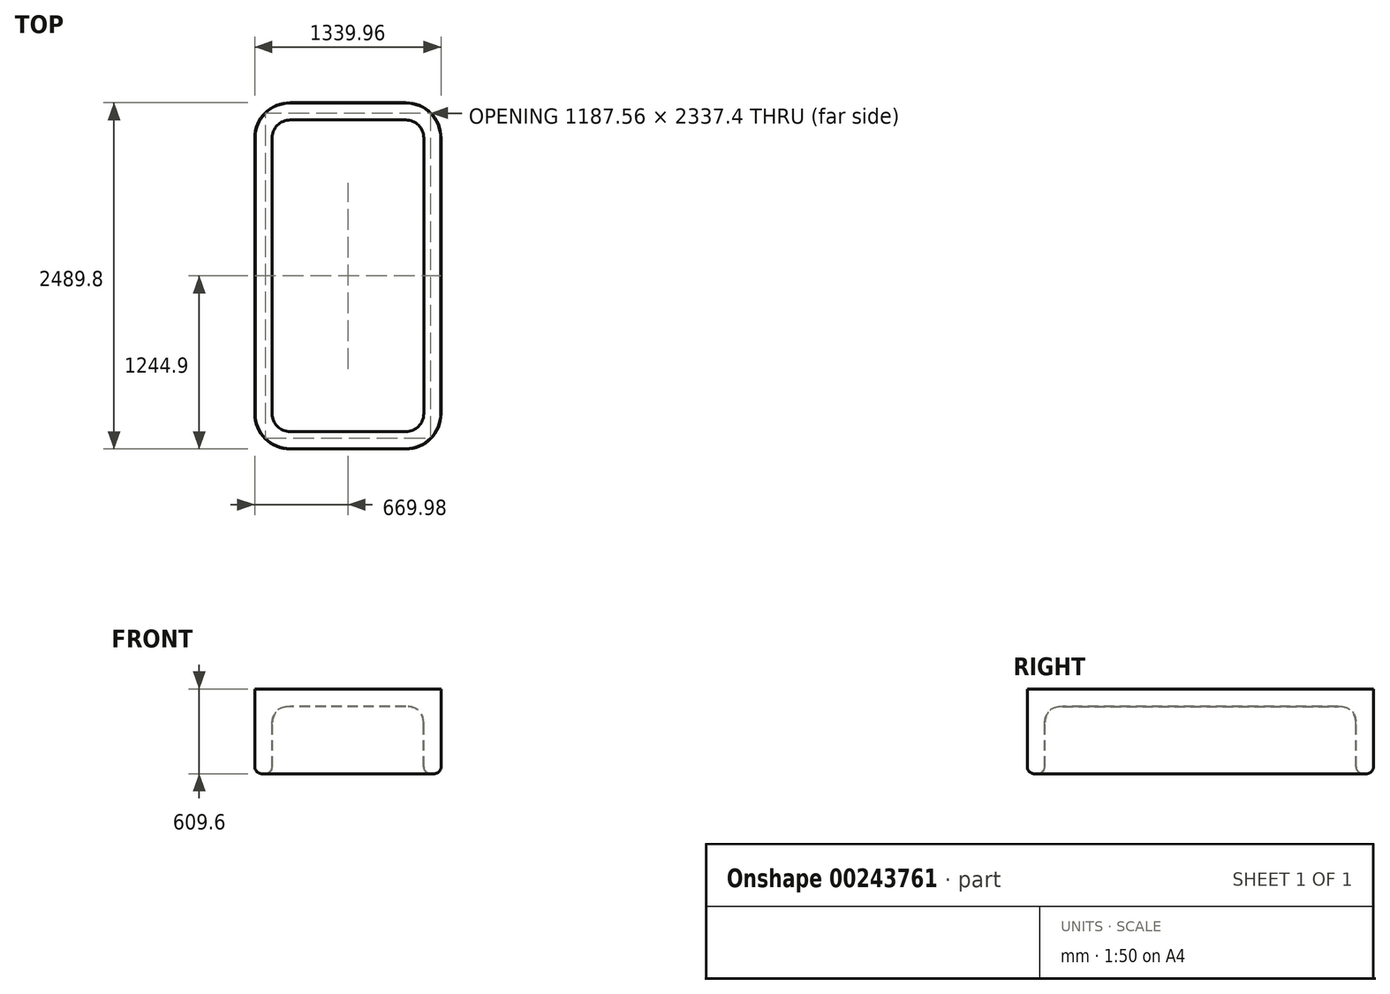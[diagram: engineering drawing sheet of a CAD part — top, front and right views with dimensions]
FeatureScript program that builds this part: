
annotation { "Feature Type Name" : "Feature", "Feature Type Description" : "" }
export const myFeature = defineFeature(function(context is Context, id is Id, definition is map)
    precondition{}
    {
        {
            var Q0;
            Q0=qCreatedBy(makeId("Top.planeOp"),FACE);
            var sketch = newSketch(context, id + "F0", { "sketchPlane" : qUnion([Q0])});
            skLineSegment(sketch, "E0.bottom", {"start": v(661.36, 66.56) * mm, "end": v(-678.6, 66.56) * mm});
            skLineSegment(sketch, "E0.top", {"start": v(661.36, 2556.36) * mm, "end": v(-678.6, 2556.36) * mm});
            skLineSegment(sketch, "E0.left", {"start": v(661.36, 66.56) * mm, "end": v(661.36, 2556.36) * mm});
            skLineSegment(sketch, "E0.right", {"start": v(-678.6, 66.56) * mm, "end": v(-678.6, 2556.36) * mm});
            skPoint(sketch, "E1.firstSnap0", {"position": v(-8.62, 66.56) * mm});
            skLineSegment(sketch, "E1.bottom", {"start": v(-8.62, 25.77) * mm, "end": v(-8.62, 25.77) * mm});
            skLineSegment(sketch, "E1.top", {"start": v(-8.62, 66.56) * mm, "end": v(-8.62, 66.56) * mm});
            skLineSegment(sketch, "E1.left", {"start": v(-8.62, 25.77) * mm, "end": v(-8.62, 66.56) * mm});
            skLineSegment(sketch, "E1.right", {"start": v(-8.62, 25.77) * mm, "end": v(-8.62, 66.56) * mm});
            skLineSegment(sketch, "E2.bottom", {"start": v(-14.24, -12.86) * mm, "end": v(-8.62, -12.86) * mm});
            skLineSegment(sketch, "E2.top", {"start": v(-14.24, 51.34) * mm, "end": v(-8.62, 51.34) * mm});
            skLineSegment(sketch, "E2.left", {"start": v(-14.24, -12.86) * mm, "end": v(-14.24, 51.34) * mm});
            skLineSegment(sketch, "E2.right", {"start": v(-8.62, -12.86) * mm, "end": v(-8.62, 51.34) * mm});
            skSolve(sketch);
        }
        {
            var Q0;
            Q0=makeQuery(id+"F0.imprint","IMPRINT",FACE,{"disambiguationData":[TD([[makeQuery(id+"F0.imprint","IMPRINT",EDGE,{"derivedFrom":sQuery(id+"F0.wireOp",EDGE,"E0.top")}),1.0]])]});
            extrude(context, id + "F1", {"entities" : qUnion([Q0]), "oppositeDirection" : true, "depth" : 609.6 * mm});
        }
        {
            var Q0;
            Q0=makeQuery(id+"F1.opExtrude","CAP_FACE",FACE,{"disambiguationData":[OSD([sQuery(id+"F0.wireOp",EDGE,"E0.bottom"),sQuery(id+"F0.wireOp",EDGE,"E0.top"),sQuery(id+"F0.wireOp",EDGE,"E0.left"),sQuery(id+"F0.wireOp",EDGE,"E0.right")])],"isStart":false});
            shell(context, id + "F2", {"entities" : qUnion([Q0]), "thickness" : 127 * mm});
        }
        {
            var Q0;
            Q0=makeQuery(id+"F2.opShell","OFFSET_EDGE",EDGE,{"disambiguationData":[OSD([sQuery(id+"F0.wireOp",EDGE,"E0.bottom"),sQuery(id+"F0.wireOp",EDGE,"E0.left")])]});
            var Q1;
            Q1=makeQuery(id+"F2.opShell","OFFSET_EDGE",EDGE,{"disambiguationData":[OSD([sQuery(id+"F0.wireOp",EDGE,"E0.top"),sQuery(id+"F0.wireOp",EDGE,"E0.left")])]});
            var Q2;
            Q2=makeQuery(id+"F2.opShell","OFFSET_EDGE",EDGE,{"disambiguationData":[OSD([sQuery(id+"F0.wireOp",EDGE,"E0.bottom"),sQuery(id+"F0.wireOp",EDGE,"E0.right")])]});
            var Q3;
            Q3=makeQuery(id+"F2.opShell","OFFSET_EDGE",EDGE,{"disambiguationData":[OSD([sQuery(id+"F0.wireOp",EDGE,"E0.top"),sQuery(id+"F0.wireOp",EDGE,"E0.right")])]});
            fillet(context, id + "F3", {"entities" : qUnion([Q0, Q1, Q2, Q3]), "radius" : 127 * mm, "tangentPropagation" : true, "allowEdgeOverflow" : false});
        }
        {
            var Q0;
            {var subQ0=sQuery(id+"F0.wireOp",EDGE,"E0.top");Q0=makeQuery(id+"F2.opShell","OFFSET_EDGE",EDGE,{"disambiguationData":[OSD([subQ0]),TDD([makeQuery(id+"F1.opExtrude","CAP_EDGE",EDGE,{"disambiguationData":[OSD([subQ0])],"isStart":true})])]});}
            fillet(context, id + "F4", {"entities" : qUnion([Q0]), "radius" : 127 * mm, "tangentPropagation" : true, "rho" : 0.5, "crossSection" : FilletCrossSection.CONIC, "allowEdgeOverflow" : false});
        }
        {
            var Q0;
            Q0=makeQuery(id+"F1.opExtrude","CAP_EDGE",EDGE,{"disambiguationData":[OSD([sQuery(id+"F0.wireOp",EDGE,"E0.top")])],"isStart":false});
            var Q1;
            Q1=makeQuery(id+"F1.opExtrude","CAP_EDGE",EDGE,{"disambiguationData":[OSD([sQuery(id+"F0.wireOp",EDGE,"E0.left")])],"isStart":false});
            var Q2;
            Q2=makeQuery(id+"F1.opExtrude","CAP_EDGE",EDGE,{"disambiguationData":[OSD([sQuery(id+"F0.wireOp",EDGE,"E0.bottom")])],"isStart":false});
            var Q3;
            Q3=makeQuery(id+"F1.opExtrude","CAP_EDGE",EDGE,{"disambiguationData":[OSD([sQuery(id+"F0.wireOp",EDGE,"E0.right")])],"isStart":false});
            var Q4;
            {var subQ0=sQuery(id+"F0.wireOp",EDGE,"E0.top");Q4=makeQuery(id+"F2.opShell","OFFSET_EDGE",EDGE,{"disambiguationData":[OSD([subQ0]),TDD([makeQuery(id+"F1.opExtrude","CAP_EDGE",EDGE,{"disambiguationData":[OSD([subQ0])],"isStart":false})])]});}
            fillet(context, id + "F5", {"entities" : qUnion([Q0, Q1, Q2, Q3, Q4]), "radius" : 50.8 * mm, "tangentPropagation" : true, "allowEdgeOverflow" : false});
        }
        {
            var Q0;
            Q0=makeQuery(id+"F1.opExtrude","SWEPT_EDGE",EDGE,{"disambiguationData":[OSD([sQuery(id+"F0.wireOp",EDGE,"E0.bottom"),sQuery(id+"F0.wireOp",EDGE,"E0.right")])]});
            var Q1;
            Q1=makeQuery(id+"F1.opExtrude","SWEPT_EDGE",EDGE,{"disambiguationData":[OSD([sQuery(id+"F0.wireOp",EDGE,"E0.bottom"),sQuery(id+"F0.wireOp",EDGE,"E0.left")])]});
            var Q2;
            Q2=makeQuery(id+"F1.opExtrude","SWEPT_EDGE",EDGE,{"disambiguationData":[OSD([sQuery(id+"F0.wireOp",EDGE,"E0.top"),sQuery(id+"F0.wireOp",EDGE,"E0.left")])]});
            var Q3;
            Q3=makeQuery(id+"F1.opExtrude","SWEPT_EDGE",EDGE,{"disambiguationData":[OSD([sQuery(id+"F0.wireOp",EDGE,"E0.top"),sQuery(id+"F0.wireOp",EDGE,"E0.right")])]});
            fillet(context, id + "F6", {"entities" : qUnion([Q0, Q1, Q2, Q3]), "radius" : 254 * mm, "tangentPropagation" : true, "allowEdgeOverflow" : false});
        }
        {
            var Q0;
            Q0=makeQuery(id+"F1.opExtrude","CAP_FACE",FACE,{"disambiguationData":[OSD([sQuery(id+"F0.wireOp",EDGE,"E0.bottom"),sQuery(id+"F0.wireOp",EDGE,"E0.top"),sQuery(id+"F0.wireOp",EDGE,"E0.left"),sQuery(id+"F0.wireOp",EDGE,"E0.right")])],"isStart":true});
            shell(context, id + "F7", {"entities" : qUnion([Q0]), "thickness" : 2.54 * mm});
        }
    });
